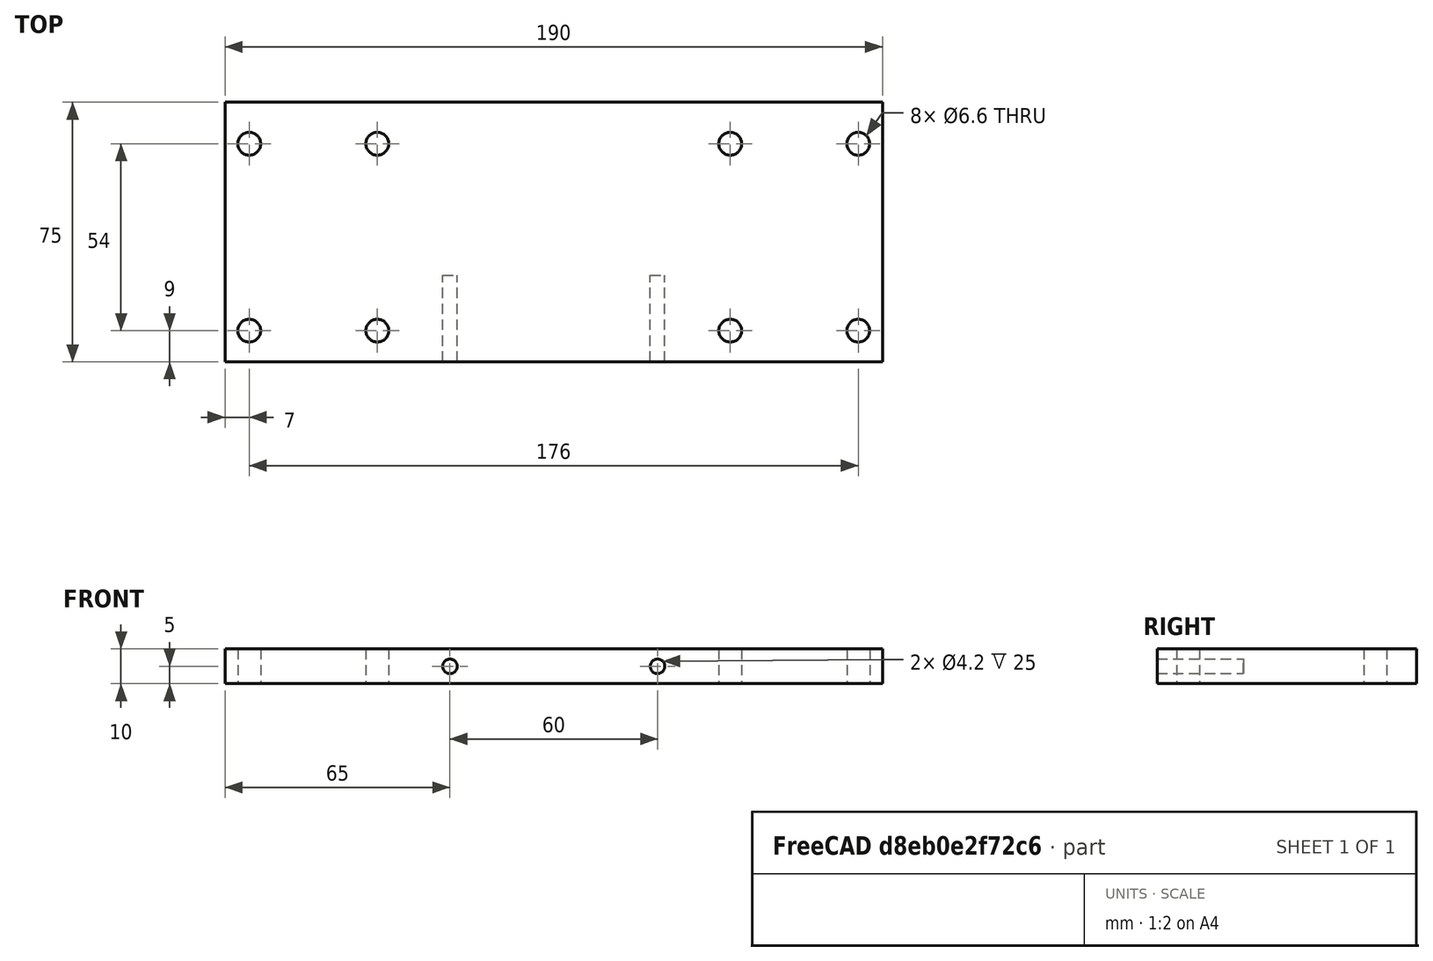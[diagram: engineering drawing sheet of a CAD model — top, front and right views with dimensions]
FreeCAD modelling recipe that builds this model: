
FCSTD DOCUMENT  (FreeCAD 0.17R13528 (Git))
Label: plate7
License: All rights reserved
LicenseURL: http://en.wikipedia.org/wiki/All_rights_reserved
objects: TechDraw::DrawViewDimension×20, PartDesign::LinearPattern×7, Sketcher::SketchObject×4, PartDesign::Hole×3, TechDraw::DrawProjGroupItem×3, PartDesign::Pad×1, PartDesign::Body×1, TechDraw::DrawSVGTemplate×1, TechDraw::DrawProjGroup×1, TechDraw::DrawViewAnnotation×1, TechDraw::DrawViewDetail×1, TechDraw::DrawPage×1
note: 20 computed .brp shape members not serialized (recipe doc carries the construction recipe); baked Part::Feature solids carry a one-line shape summary decoded from their .brp

FEATURE [Sketcher::SketchObject] Sketch
  MapMode = 5
  Support = -> [XY_Plane]
  sketch-geometry (4):
    g0: LineSegment StartX=0 StartY=0 StartZ=0 EndX=190 EndY=0 EndZ=0
    g1: LineSegment StartX=190 StartY=0 StartZ=0 EndX=190 EndY=75 EndZ=0
    g2: LineSegment StartX=190 StartY=75 StartZ=0 EndX=0 EndY=75 EndZ=0
    g3: LineSegment StartX=0 StartY=75 StartZ=0 EndX=0 EndY=0 EndZ=0
  constraints (11):
    c: Coincident(g0,g1)
    c: Coincident(g1,g2)
    c: Coincident(g2,g3)
    c: Coincident(g3,g0)
    c: Horizontal(g0)
    c: Horizontal(g2)
    c: Vertical(g1)
    c: Vertical(g3)
    c: Coincident(g0,g-1)
    c: DistanceX(g0,g0) = 190
    c: DistanceY(g3,g3) = 75
FEATURE [PartDesign::Pad] Pad
  Length = 10
  Length2 = 100
  Profile = -> Sketch
  Type = 0
FEATURE [Sketcher::SketchObject] Sketch001
  MapMode = 5
  Placement = pos=(0,0,10) rot=(0,0,1;0rad)
  Support = -> [Pad]
  sketch-geometry (1):
    g0: Circle CenterX=7 CenterY=9 CenterZ=0 NormalX=0 NormalY=0 NormalZ=1 AngleXU=0 Radius=3.29825
  constraints (2):
    c: Distance(g0,g-1) = 9
    c: Distance(g0,g-2) = 7
FEATURE [PartDesign::Hole] Hole
  BaseFeature = -> Pad
  Depth = 25
  DepthType = 1
  Diameter = 6.6
  DrillPoint = 0
  DrillPointAngle = 118
  HoleCutCountersinkAngle = 90
  HoleCutDepth = 0
  HoleCutDiameter = 6
  HoleCutType = 0
  ModelActualThread = false
  Profile = -> Sketch001
  Tapered = false
  TaperedAngle = 90
  ThreadAngle = 0
  ThreadClass = 0
  ThreadCutOffInner = 0
  ThreadCutOffOuter = 0
  ThreadDirection = 0
  ThreadFit = 0
  ThreadPitch = 0
  ThreadSize = 7
  ThreadType = 1
  Threaded = false
FEATURE [PartDesign::LinearPattern] LinearPattern
  BaseFeature = -> Hole
  Direction = -> Sketch001 [H_Axis]
  Length = 37
  Occurrences = 2
  Originals = -> [Hole]
FEATURE [PartDesign::LinearPattern] LinearPattern001
  BaseFeature = -> LinearPattern
  Direction = -> Sketch001 [H_Axis]
  Length = 139
  Occurrences = 2
  Originals = -> [Hole]
FEATURE [PartDesign::LinearPattern] LinearPattern002
  BaseFeature = -> LinearPattern001
  Direction = -> Sketch001 [H_Axis]
  Length = 176
  Occurrences = 2
  Originals = -> [Hole]
FEATURE [Sketcher::SketchObject] Sketch002
  MapMode = 5
  Placement = pos=(0,0,10) rot=(0,0,1;0rad)
  Support = -> [LinearPattern002]
  sketch-geometry (1):
    g0: Circle CenterX=7 CenterY=63 CenterZ=0 NormalX=0 NormalY=0 NormalZ=1 AngleXU=0 Radius=4.03844
  constraints (2):
    c: Distance(g0,g-2) = 7
    c: Distance(g0,g-1) = 63
FEATURE [PartDesign::Hole] Hole001
  BaseFeature = -> LinearPattern002
  Depth = 25
  DepthType = 1
  Diameter = 6.6
  DrillPoint = 0
  DrillPointAngle = 118
  HoleCutCountersinkAngle = 90
  HoleCutDepth = 0
  HoleCutDiameter = 6
  HoleCutType = 0
  ModelActualThread = false
  Profile = -> Sketch002
  Tapered = false
  TaperedAngle = 90
  ThreadAngle = 0
  ThreadClass = 0
  ThreadCutOffInner = 0
  ThreadCutOffOuter = 0
  ThreadDirection = 0
  ThreadFit = 0
  ThreadPitch = 0
  ThreadSize = 7
  ThreadType = 1
  Threaded = false
FEATURE [PartDesign::LinearPattern] LinearPattern003
  BaseFeature = -> Hole001
  Direction = -> Sketch002 [H_Axis]
  Length = 37
  Occurrences = 2
  Originals = -> [Hole001]
FEATURE [PartDesign::LinearPattern] LinearPattern004
  BaseFeature = -> LinearPattern003
  Direction = -> Sketch002 [H_Axis]
  Length = 139
  Occurrences = 2
  Originals = -> [Hole001]
FEATURE [PartDesign::LinearPattern] LinearPattern005
  BaseFeature = -> LinearPattern004
  Direction = -> Sketch002 [H_Axis]
  Length = 176
  Occurrences = 2
  Originals = -> [Hole001]
FEATURE [Sketcher::SketchObject] Sketch003
  MapMode = 5
  Placement = pos=(0,0,0) rot=(1,0,0;1.5708rad)
  Support = -> [LinearPattern005]
  sketch-geometry (1):
    g0: Circle CenterX=65 CenterY=5 CenterZ=0 NormalX=0 NormalY=0 NormalZ=1 AngleXU=0 Radius=3.79368
  constraints (2):
    c: Distance(g0,g-2) = 65
    c: Distance(g0,g-1) = 5
FEATURE [PartDesign::Hole] Hole002
  BaseFeature = -> LinearPattern005
  Depth = 25
  DepthType = 0
  Diameter = 4.2
  DrillPoint = 0
  DrillPointAngle = 118
  HoleCutCountersinkAngle = 90
  HoleCutDepth = 0
  HoleCutDiameter = 5
  HoleCutType = 0
  ModelActualThread = false
  Profile = -> Sketch003
  Tapered = false
  TaperedAngle = 90
  ThreadAngle = 60
  ThreadClass = 0
  ThreadCutOffInner = 0.0866025
  ThreadCutOffOuter = 0.173205
  ThreadDirection = 1
  ThreadFit = 0
  ThreadPitch = 0.8
  ThreadSize = 6
  ThreadType = 1
  Threaded = true
FEATURE [PartDesign::LinearPattern] LinearPattern006
  BaseFeature = -> Hole002
  Direction = -> Sketch003 [H_Axis]
  Length = 60
  Occurrences = 2
  Originals = -> [Hole002]
FEATURE [PartDesign::Body] Body
  Group = -> [Sketch,Pad,Sketch001,Hole,LinearPattern,LinearPattern001,LinearPattern002,Sketch002,Hole001,LinearPattern003,LinearPattern004,LinearPattern005,Sketch003,Hole002,LinearPattern006]
  Origin = -> Origin
  Tip = -> LinearPattern006
FEATURE [TechDraw::DrawSVGTemplate] Template
  EditableTexts = Designed_by_Name=Lukas Winter; FC-Date=28.08.2018; FC-SC=1:1; FC-SH=1/1; FC-Title=COSI Measure v1.0; Subtitle=Mechanical assembly - plate 7
  Height = 210
  Orientation = 1
  Width = 297
FEATURE [TechDraw::DrawProjGroupItem] ProjItem  label="Front"
  CoarseView = false
  Direction = (0,-1,0)
  Focus = 100
  HardHidden = false
  IsoCount = 0
  IsoHidden = false
  IsoVisible = false
  LockPosition = false
  Perspective = false
  Rotation = 0
  RotationVector = (1,0,0)
  ScaleType = 0
  SeamHidden = false
  SeamVisible = false
  SmoothHidden = false
  SmoothVisible = false
  Source = -> [Body]
  Type = 0
  X = -161.875
  Y = 61.25
FEATURE [TechDraw::DrawProjGroupItem] ProjItem001  label="Bottom"
  CoarseView = false
  Direction = (0,0,-1)
  Focus = 100
  HardHidden = false
  IsoCount = 0
  IsoHidden = false
  IsoVisible = false
  LockPosition = false
  Perspective = false
  Rotation = 0
  RotationVector = (1,0,0)
  ScaleType = 0
  SeamHidden = false
  SeamVisible = false
  SmoothHidden = false
  SmoothVisible = false
  Source = -> [Body]
  Type = 5
  X = 0
  Y = -62.4248
FEATURE [TechDraw::DrawProjGroupItem] ProjItem002  label="Right"
  CoarseView = false
  Direction = (1,0,0)
  Focus = 100
  HardHidden = false
  IsoCount = 0
  IsoHidden = false
  IsoVisible = false
  LockPosition = false
  Perspective = false
  Rotation = 0
  RotationVector = (0,-1,0)
  ScaleType = 0
  SeamHidden = false
  SeamVisible = false
  SmoothHidden = false
  SmoothVisible = false
  Source = -> [Body]
  Type = 2
  X = 135.624
  Y = 0
FEATURE [TechDraw::DrawProjGroup] ProjGroup
  Anchor = -> ProjItem
  AutoDistribute = true
  CubeDirs = (1) [(0,0,0)]
  CubeRotations = (1) [(0,0,0)]
  LockPosition = false
  ProjectionType = 2
  Rotation = 0
  ScaleType = 0
  Source = -> [Body]
  Views = -> [ProjItem,ProjItem001,ProjItem002]
  X = 111.782
  Y = 168.981
  spacingX = 15
  spacingY = 15
FEATURE [TechDraw::DrawViewDimension] Dimension
  FormatSpec = %.2f
  LockPosition = false
  MeasureType = 1
  References2D = -> [ProjItem002]
  Rotation = 0
  ScaleType = 0
  Type = 2
  X = 27.2171
  Y = -28.1638
FEATURE [TechDraw::DrawViewDimension] Dimension001
  FormatSpec = %.2f
  LockPosition = false
  MeasureType = 1
  References2D = -> [ProjItem002]
  Rotation = 0
  ScaleType = 0
  Type = 1
  X = -0.946681
  Y = 14.2002
FEATURE [TechDraw::DrawViewDimension] Dimension002
  FormatSpec = %.2f
  LockPosition = false
  MeasureType = 1
  References2D = -> [ProjItem]
  Rotation = 0
  ScaleType = 0
  Type = 1
  X = 0.710011
  Y = 27.125
FEATURE [TechDraw::DrawViewDimension] Dimension003
  FormatSpec = %.2f
  LockPosition = false
  MeasureType = 1
  References2D = -> [ProjItem001]
  Rotation = 0
  ScaleType = 0
  Type = 5
  X = 0
  Y = 0
FEATURE [TechDraw::DrawViewDimension] Dimension006
  FormatSpec = %.2f
  LockPosition = false
  MeasureType = 1
  References2D = -> [ProjItem001]
  Rotation = 0
  ScaleType = 0
  Type = 1
  X = -77.9938
  Y = 7.77778
FEATURE [TechDraw::DrawViewDimension] Dimension007
  FormatSpec = %.2f
  LockPosition = false
  MeasureType = 1
  References2D = -> [ProjItem001]
  Rotation = 0
  ScaleType = 0
  Type = 1
  X = -70
  Y = 19.2284
FEATURE [TechDraw::DrawViewDimension] Dimension008
  FormatSpec = %.2f
  LockPosition = false
  MeasureType = 1
  References2D = -> [ProjItem001]
  Rotation = 0
  ScaleType = 0
  Type = 1
  X = 0.648148
  Y = 19.0123
FEATURE [TechDraw::DrawViewDimension] Dimension009
  FormatSpec = %.2f
  LockPosition = false
  MeasureType = 1
  References2D = -> [ProjItem001]
  Rotation = 0
  ScaleType = 0
  Type = 1
  X = 69.784
  Y = 18.7963
FEATURE [TechDraw::DrawViewDimension] Dimension010
  FormatSpec = %.2f
  LockPosition = false
  MeasureType = 1
  References2D = -> [ProjItem001]
  Rotation = 0
  ScaleType = 0
  Type = 2
  X = 101.543
  Y = 18.1481
FEATURE [TechDraw::DrawViewDimension] Dimension011
  FormatSpec = %.2f
  LockPosition = false
  MeasureType = 1
  References2D = -> [ProjItem001]
  Rotation = 0
  ScaleType = 0
  Type = 2
  X = 102.623
  Y = -15.7716
FEATURE [TechDraw::DrawViewDimension] Dimension012
  FormatSpec = %.2f
  LockPosition = false
  MeasureType = 1
  References2D = -> [ProjItem001]
  Rotation = 0
  ScaleType = 0
  Type = 1
  X = 77.7778
  Y = 7.56173
FEATURE [TechDraw::DrawViewDimension] Dimension013
  FormatSpec = %.2f
  LockPosition = false
  MeasureType = 1
  References2D = -> [ProjItem001]
  Rotation = 0
  ScaleType = 0
  Type = 2
  X = 37.8086
  Y = -0.864198
FEATURE [TechDraw::DrawViewDimension] Dimension014
  FormatSpec = %.2f
  LockPosition = false
  MeasureType = 1
  References2D = -> [ProjItem001]
  Rotation = 0
  ScaleType = 0
  Type = 1
  X = -79.9383
  Y = -13.8272
FEATURE [TechDraw::DrawViewDimension] Dimension015
  FormatSpec = %.2f
  LockPosition = false
  MeasureType = 1
  References2D = -> [ProjItem001]
  Rotation = 0
  ScaleType = 0
  Type = 1
  X = -68.7037
  Y = -31.1111
FEATURE [TechDraw::DrawViewDimension] Dimension016
  FormatSpec = %.2f
  LockPosition = false
  MeasureType = 1
  References2D = -> [ProjItem001]
  Rotation = 0
  ScaleType = 0
  Type = 1
  X = -1.05024
  Y = -31.2071
FEATURE [TechDraw::DrawViewDimension] Dimension017
  FormatSpec = %.2f
  LockPosition = false
  MeasureType = 1
  References2D = -> [ProjItem001]
  Rotation = 0
  ScaleType = 0
  Type = 1
  X = 71.0011
  Y = -31.1616
FEATURE [TechDraw::DrawViewAnnotation] Annotation001
  Font = osifont
  LineSpace = 80
  LockPosition = false
  MaxWidth = -1
  Rotation = 0
  ScaleType = 0
  Text = Thread M5x20mm
  TextSize = 4
  TextStyle = 0
  X = 251.54
  Y = 133.747
FEATURE [TechDraw::DrawViewDetail] Detail  label="Detail 1"
  AnchorPoint = (30,0,0)
  BaseView = -> ProjItem
  CoarseView = false
  Direction = (0,-1,0)
  Focus = 100
  HardHidden = false
  IsoCount = 0
  IsoHidden = false
  IsoVisible = false
  LockPosition = false
  Perspective = false
  Radius = 10
  Reference = 1
  Rotation = 0
  ScaleType = 0
  SeamHidden = false
  SeamVisible = false
  SmoothHidden = false
  SmoothVisible = false
  Source = -> [Body]
  X = 252.016
  Y = 114.282
FEATURE [TechDraw::DrawViewDimension] Dimension018
  FormatSpec = %.2f
  LockPosition = false
  MeasureType = 1
  References2D = -> [ProjItem]
  Rotation = 0
  ScaleType = 0
  Type = 2
  X = -25.0133
  Y = 20.5333
FEATURE [TechDraw::DrawViewDimension] Dimension019
  FormatSpec = %.2f
  LockPosition = false
  MeasureType = 1
  References2D = -> [ProjItem]
  Rotation = 0
  ScaleType = 0
  Type = 1
  X = -67.2
  Y = 12.32
FEATURE [TechDraw::DrawViewDimension] Dimension020
  FormatSpec = %.2f
  LockPosition = false
  MeasureType = 1
  References2D = -> [ProjItem]
  Rotation = 0
  ScaleType = 0
  Type = 1
  X = 0
  Y = 12.32
FEATURE [TechDraw::DrawViewDimension] Dimension021
  FormatSpec = %.2f
  LockPosition = false
  MeasureType = 1
  References2D = -> [ProjItem]
  Rotation = 0
  ScaleType = 0
  Type = 1
  X = 66.4533
  Y = 11.9467
FEATURE [TechDraw::DrawPage] Page
  KeepUpdated = true
  ProjectionType = 0
  Template = -> Template
  Views = -> [ProjGroup,Dimension,Dimension001,Dimension002,Dimension003,Dimension006,Dimension007,Dimension008,Dimension009,Dimension010,Dimension011,Dimension012,Dimension013,Dimension014,Dimension015,Dimension016,Dimension017,Annotation001,Detail,Dimension018,Dimension019,Dimension020,Dimension021]
